# Revit family: ZENITH LED
name_source: partatom
category: Осветительные приборы
revit_build: Autodesk Revit 2016 (Build: 20161004_0715(x64)
units: mm (PartAtom-declared; Revit-internal decimal feet)

## family parameters
Источник света = Нет
Общий = Нет
Основа = Грань
При загрузке вырезать с полостями = Нет
Размер круглого соединителя = Использовать диаметр
Тип детали = Нормальный
Точка расчета площади = Нет

## types (1)
- ZENITH LED
    ADSK_Единица измерения = Шт.
    ADSK_Завод-изготовитель = ООО МГК Световые технологии
    ADSK_Классификация нагрузок = Прочее
    ADSK_Код изделия = 1226000200
    ADSK_Количество фаз = 1
    ADSK_Количество фаз числовое = 1
    ADSK_Коэффициент мощности = 0.98
    ADSK_Масса = 9.1
    ADSK_Наименование = Светильники серии ZENITH LED Ex предназначены для наружного и внутреннего освещения взрывоопасных зон всех классов помещений и предприятий нефтегазовой, нефтехимической отрасли, а также подземных выработок шахт, рудников, опасных в отношении рудничного газа и (или) горючей пыли. Оптимальное решение для замены Ex-светильников с натриевыми и металлгалогенными лампами до 150 Вт
    ADSK_Напряжение = 230 В
    ADSK_Номинальная мощность = 0 кВт
    ADSK_Полная мощность = 0 кВ·А
    ADSK_Размер_Высота = 240 мм
    ADSK_Размер_Ширина = 243 мм
    ADSK_Ток = 0 А
    ADSK_Энергоэффективность = 115 лм/Вт
    IP Class = IP66
    L = 200 мм
    URL = https://ltcompany.com
    Блок аварийного питания = Нет
    Выбор ИС = IES ZENITH LED Ex : ZENITH LED 100 D270 B Ex
    Группа модели = Светильники
    Да = Нет
    Изготовитель = ООО МГК Световые технологии
    Класс Защиты = I
    Класс пожароопасности = П-II,IIа
    Климатическая зона = УХЛ1
    Код по классификатору = D5020200
    Корпус = Cерый металл матовый
    Крепление.лира = Да
    Нет = Нет
    Область использования = Нефтегазовая промышленность
    Описание = Светильники серии ZENITH LED Ex предназначены для наружного и внутреннего освещения взрывоопасных зон всех классов помещений и предприятий нефтегазовой, нефтехимической отрасли, а также подземных выработок шахт, рудников, опасных в отношении рудничного газа и (или) горючей пыли. Оптимальное решение для замены Ex-светильников с натриевыми и металлгалогенными лампами до 150 Вт
    Отметка по умолчанию = 0 мм
    Плафон = Плафон самосвечение
    Полная установленная мощность = 0 кВ·А
    Полусферический рассеиватель = Плафон прозрачный
    Рассеиватель.полусфера = Да
    Тип ИС = LED
    Тип ПРА = Драйвер
    Тип продукции = Светильник
